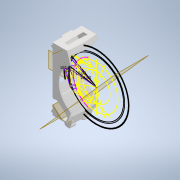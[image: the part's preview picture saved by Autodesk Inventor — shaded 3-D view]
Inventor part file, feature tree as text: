
AUTODESK INVENTOR PART (.ipt)
format: ipt  version: 2022 (Build 260153000, 153)  size: 1,890,816 bytes
history: native  units: mm
features: reference x91, sketch x37, projected_geometry x36, other x31, extrude x31, fillet x23, revolve x5, chamfer x5, mirror x3
ambient origin geometry x8: Origin, YZ Plane, XZ Plane, XY Plane, X Axis, Y Axis, Z Axis, Center Point
bodies: Body1 (feature_tree)
feature tree (262):
  other  "Твердое тело1"
  sketch  "Эскиз1"
  extrude  "Выдавливание1"  Depth=3.490659mm
  extrude  "Выдавливание2"  Depth=3.490659mm
  extrude  "Выдавливание3"  Depth=1.0mm
  sketch  "Эскиз5"
  extrude  "Выдавливание4"  Depth=1.0mm
  extrude  "Выдавливание5"  Depth=4.537856mm
  other  "РабПлоскость1"
  extrude  "Выдавливание6"  Depth=4.537856mm
  extrude  "Выдавливание7"  Depth=0.5mm
  extrude  "Выдавливание8"  Depth=18.69mm TaperAngle=0.0deg
  fillet  "Сопряжение2"  Radius=20.45mm
  extrude  "Выдавливание9"  Depth=1.5mm TaperAngle=0.0deg
  extrude  "Выдавливание10"  Depth=1.5mm
  fillet  "Сопряжение3"  Radius=3.0mm
  fillet  "Сопряжение4"  [1 undecoded]
  extrude  "Выдавливание11"  Depth=9.162979mm
  fillet  "Сопряжение6"  Radius=2.0mm
  fillet  "Сопряжение7"  Radius=28.843311mm
  extrude  "Выдавливание12"  Depth=1.5mm
  extrude  "Выдавливание13"  Depth=1.2mm
  fillet  "Сопряжение8"  Radius=20.69mm
  revolve  "Вращение1"
  fillet  "Сопряжение9"  Radius=11.0mm
  fillet  "Сопряжение10"  Radius=1.3mm
  extrude  "Выдавливание14"  Depth=14.5mm
  fillet  "Сопряжение11"  Radius=11.0mm
  fillet  "Сопряжение12"  Radius=9.0mm
  fillet  "Сопряжение13"  Radius=9.0mm
  chamfer  "Фаска1"  Distance=2.0mm
  extrude  "Выдавливание15"  Depth=1.0mm
  fillet  "Сопряжение14"  Radius=0.3mm
  other  "РабПлоскость4"
  revolve  "Вращение4"
  extrude  "Выдавливание28"  Depth=0.3mm
  chamfer  "Фаска3"  Distance=0.3mm
  fillet  "Сопряжение30"  Radius=0.3mm
  chamfer  "Фаска5"  Distance=25.0mm
  extrude  "Выдавливание31"  Depth=0.3mm TaperAngle=0.0deg
  extrude  "Выдавливание32"  Depth=2.0mm TaperAngle=0.0deg
  chamfer  "Фаска6"  Distance=10.0mm
  other  "РабПлоскость5"
  mirror  "Зеркальное отражение14"
  extrude  "Выдавливание33"  Depth=1.0mm
  mirror  "Зеркальное отражение15"
  other  "РабПлоскость9"
  extrude  "Выдавливание34"  Depth=0.7mm
  fillet  "Сопряжение31"  Radius=0.7mm
  fillet  "Сопряжение32"  Radius=0.3mm
  extrude  "Выдавливание35"  Depth=0.2mm TaperAngle=0.0deg
  extrude  "Выдавливание36"  Depth=0.2mm TaperAngle=0.0deg
  extrude  "Выдавливание37"  Depth=0.5mm
  mirror  "Зеркальное отражение16"
  extrude  "Выдавливание38"  Depth=3.5mm
  extrude  "Выдавливание39"  Depth=0.8mm
  chamfer  "Фаска7"  Distance=2.0mm
  fillet  "Сопряжение33"  Radius=2.0mm
  revolve  "Вращение5"
  fillet  "Сопряжение34"  Radius=200.0mm
  extrude  "Выдавливание40"  Depth=0.5mm
  extrude  "Выдавливание41"  Depth=0.5mm
  fillet  "Сопряжение35"  Radius=2.0mm
  extrude  "Выдавливание42"  Depth=2.0mm TaperAngle=0.0deg
  extrude  "Выдавливание43"  Depth=0.5mm
  extrude  "Выдавливание44"  Depth=3.490659mm
  sketch  "Эскиз53"
  other  "РабПлоскость10"
  revolve  "Вращение6"
  revolve  "Вращение7"
  fillet  "Сопряжение36"  Radius=2.0mm
  fillet  "Сопряжение37"  [1 undecoded]
  fillet  "Сопряжение38"  Radius=0.7mm
  extrude  "Выдавливание45"  Depth=2.0mm
  fillet  "Сопряжение39"  Radius=0.8mm
  fillet  "Сопряжение40"  Radius=3.0mm
  reference  "Ссылка1"
  reference  "Ссылка2"
  reference  "Ссылка3"
  reference  "Ссылка4"
  reference  "Ссылка5"
  reference  "Ссылка6"
  reference  "Ссылка7"
  reference  "Ссылка8"
  reference  "Ссылка9"
  reference  "Ссылка10"
  reference  "Ссылка11"
  reference  "Ссылка12"
  reference  "Ссылка13"
  reference  "Ссылка14"
  reference  "Ссылка15"
  reference  "Ссылка16"
  reference  "Ссылка17"
  reference  "Ссылка18"
  reference  "Ссылка19"
  reference  "Ссылка20"
  reference  "Ссылка21"
  reference  "Ссылка22"
  reference  "Ссылка23"
  reference  "Ссылка24"
  reference  "Ссылка25"
  sketch  "Эскиз2"
  reference  "Ссылка26"
  reference  "Ссылка27"
  reference  "Ссылка28"
  reference  "Ссылка29"
  reference  "Ссылка30"
  sketch  "Эскиз3"
  projected_geometry  "Спроецированная петля1"
  projected_geometry  "Спроецированная петля2"
  reference  "Ссылка31"
  sketch  "Эскиз4"
  projected_geometry  "Спроецированная петля3"
  reference  "Ссылка32"
  projected_geometry  "Спроецированная петля4"
  projected_geometry  "Спроецированная петля5"
  reference  "Ссылка33"
  reference  "Ссылка34"
  reference  "Ссылка35"
  reference  "Ссылка47"
  sketch  "Эскиз6"
  projected_geometry  "Спроецированная петля6"
  sketch  "Эскиз7"
  projected_geometry  "Спроецированная петля7"
  sketch  "Эскиз8"
  reference  "Ссылка51"
  projected_geometry  "Спроецированная петля8"
  sketch  "Эскиз10"
  reference  "Ссылка54"
  reference  "Ссылка55"
  reference  "Ссылка56"
  reference  "Ссылка57"
  reference  "Ссылка58"
  sketch  "Эскиз11"
  projected_geometry  "Спроецированная петля9"
  sketch  "Эскиз12"
  projected_geometry  "Спроецированная петля10"
  reference  "Ссылка59"
  reference  "Ссылка60"
  reference  "Ссылка61"
  sketch  "Эскиз13"
  reference  "Ссылка62"
  reference  "Ссылка63"
  reference  "Ссылка64"
  reference  "Ссылка65"
  sketch  "Эскиз14"
  reference  "Ссылка66"
  projected_geometry  "Спроецированная петля11"
  sketch  "Эскиз15"
  projected_geometry  "Спроецированная петля12"
  sketch  "Эскиз16"
  reference  "Ссылка67"
  reference  "Ссылка68"
  reference  "Ссылка69"
  reference  "Ссылка70"
  reference  "Ссылка71"
  reference  "Ссылка72"
  sketch  "Эскиз17"
  reference  "Ссылка73"
  reference  "Ссылка74"
  projected_geometry  "Спроецированная петля13"
  projected_geometry  "Спроецированная петля14"
  reference  "Ссылка75"
  reference  "Ссылка76"
  sketch  "Эскиз18"
  reference  "Ссылка77"
  reference  "Ссылка78"
  reference  "Ссылка79"
  reference  "Ссылка80"
  reference  "Ссылка81"
  reference  "Ссылка82"
  reference  "Ссылка83"
  reference  "Ссылка84"
  sketch  "Эскиз33"
  projected_geometry  "Спроецированная петля41"
  projected_geometry  "Спроецированная петля42"
  projected_geometry  "Спроецированная петля43"
  reference  "Ссылка117"
  reference  "Ссылка118"
  reference  "Ссылка119"
  reference  "Ссылка120"
  reference  "Ссылка121"
  reference  "Ссылка122"
  sketch  "Эскиз38"
  sketch  "Эскиз39"
  projected_geometry  "Спроецированная петля46"
  projected_geometry  "Спроецированная петля47"
  other  "РабПлоскость6"
  sketch  "Эскиз40"
  reference  "Ссылка123"
  reference  "Ссылка124"
  reference  "Ссылка125"
  reference  "Ссылка126"
  reference  "Ссылка127"
  sketch  "Эскиз41"
  projected_geometry  "Спроецированная петля48"
  reference  "Ссылка128"
  sketch  "Эскиз42"
  projected_geometry  "Спроецированная петля49"
  reference  "Ссылка129"
  reference  "Ссылка130"
  projected_geometry  "Спроецированная петля50"
  reference  "Ссылка131"
  reference  "Ссылка132"
  reference  "Ссылка133"
  reference  "Ссылка134"
  sketch  "Эскиз43"
  projected_geometry  "Спроецированная петля51"
  sketch  "Эскиз44"
  projected_geometry  "Спроецированная петля52"
  sketch  "Эскиз45"
  projected_geometry  "Спроецированная петля53"
  sketch  "Эскиз46"
  reference  "Ссылка135"
  projected_geometry  "Спроецированная петля54"
  sketch  "Эскиз47"
  sketch  "Эскиз48"
  reference  "Ссылка136"
  sketch  "Эскиз49"
  projected_geometry  "Спроецированная петля55"
  projected_geometry  "Спроецированная петля56"
  reference  "Ссылка137"
  sketch  "Эскиз50"
  sketch  "Эскиз51"
  projected_geometry  "Спроецированная петля57"
  projected_geometry  "Спроецированная петля58"
  sketch  "Эскиз52"
  projected_geometry  "Спроецированная петля59"
  reference  "Ссылка138"
  reference  "Ссылка139"
  sketch  "Эскиз54"
  projected_geometry  "Спроецированная петля60"
  projected_geometry  "Спроецированная петля61"
  sketch  "Эскиз55"
  projected_geometry  "Спроецированная петля62"
  sketch  "Эскиз56"
  projected_geometry  "Спроецированная петля63"
  projected_geometry  "Спроецированная петля64"
  other  "<userpath>\Documents\Git\MZCAT_2024\MZCAT_2.iam"
  other  "MZCAT_2.iam"
  other  "lidar_krestovina:1"
  other  "shatun_lidar:1"
  other  "stabilisator_plan:1"
  other  "OCS-D008 B:3"
  other  "commutationCATboard:1"
  other  "CAT_protector:1"
  other  "OCS-D008 B:2"
  other  "<userpath>\Documents\Git\MZCAT_2024_construction\MZCAT_2024_RPI_2\MZCAT_4.iam"
  other  "MZCAT_4.iam"
  other  "vydacha_pusher:2"
  other  "FastBattery:1"
  other  "metal_cap:1"
  other  "base plate:1"
  other  "base plate:2"
  other  "<userpath>\Documents\Git\MZCAT_2024\MZCAT_3.iam"
  other  "MZCAT_3.iam"
  other  "akkum_cup:1"
  other  "vydacha_slide:1"
  other  "Camera_module_3_wide:1"
  other  "Camera_module_3_wide:2"
  other  "Camera_module_3_wide_model_simple:1"
  other  "<userpath>\Documents\Git\MZCAT_2024_construction\MZCAT_2024_RPI\MZCAT_4.iam"
note: 2 required parameter values undecoded (feature->parameter linkage not recoverable at this tier; creation-order binding heuristic only, values carry confidence <= 0.55)
